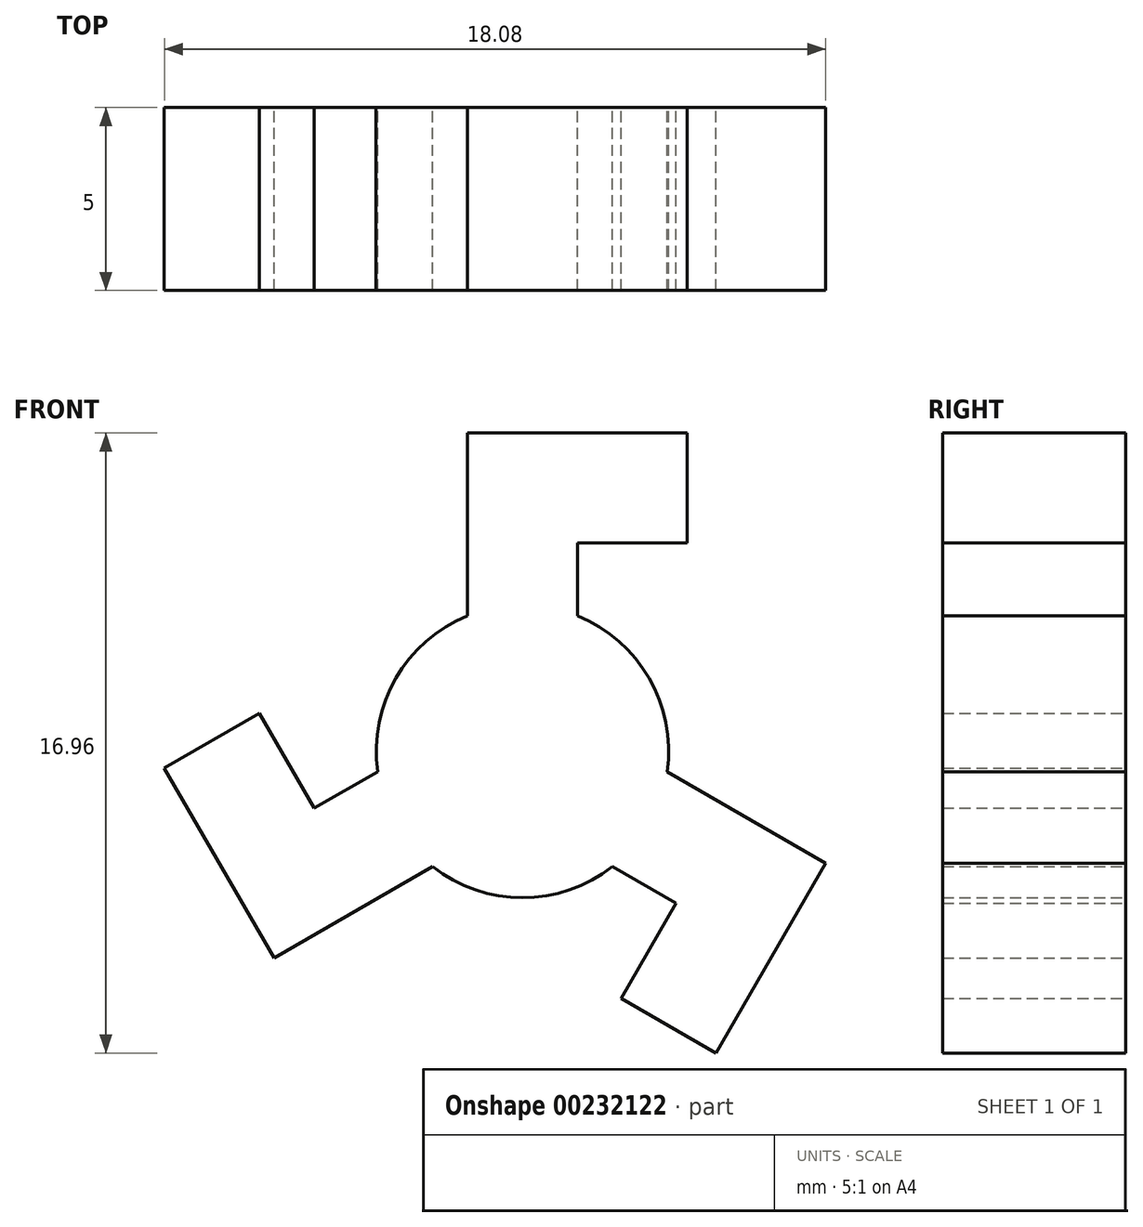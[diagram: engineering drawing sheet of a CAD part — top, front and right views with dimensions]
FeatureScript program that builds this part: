
annotation { "Feature Type Name" : "Feature", "Feature Type Description" : "" }
export const myFeature = defineFeature(function(context is Context, id is Id, definition is map)
    precondition{}
    {
        {
            var Q0;
            Q0=qCreatedBy(makeId("Front.planeOp"),FACE);
            var sketch = newSketch(context, id + "F0", { "sketchPlane" : qUnion([Q0])});
            skArc(sketch, "E0", {"start": v(-1.5, 3.7) * mm, "mid": v(-3.46, 2) * mm, "end": v(-3.96, -0.56) * mm});
            skLineSegment(sketch, "E1.left", {"start": v(-1.5, 8.4) * mm, "end": v(-1.5, 3.7) * mm});
            skLineSegment(sketch, "E1.right", {"start": v(1.5, 5.7) * mm, "end": v(1.5, 3.7) * mm});
            skPoint(sketch, "E1.middle", {"position": v(0, 4) * mm});
            skLineSegment(sketch, "E2.bottom", {"start": v(1.5, 5.7) * mm, "end": v(4.5, 5.7) * mm});
            skLineSegment(sketch, "E2.top", {"start": v(-1.5, 8.7) * mm, "end": v(4.5, 8.7) * mm});
            skLineSegment(sketch, "E2.left", {"start": v(-1.5, 8.4) * mm, "end": v(-1.5, 8.7) * mm});
            skLineSegment(sketch, "E2.right", {"start": v(4.5, 5.7) * mm, "end": v(4.5, 8.7) * mm});
            skPoint(sketch, "E2.middle", {"position": v(1.5, 7.2) * mm});
            skPoint(sketch, "E1.top.start.orphan", {"position": v(-1.5, 0.8) * mm});
            skPoint(sketch, "E3.orphan", {"position": v(1.5, -0.4) * mm});
            skPoint(sketch, "E4.orphan", {"position": v(-1.5, 5.7) * mm});
            skLineSegment(sketch, "E5.1.0", {"start": v(-6.8, -5.65) * mm, "end": v(-9.8, -0.46) * mm});
            skLineSegment(sketch, "E5.1.1", {"start": v(-7.2, 1.04) * mm, "end": v(-9.8, -0.46) * mm});
            skPoint(sketch, "E5.1.2", {"position": v(-7, -2.3) * mm});
            skLineSegment(sketch, "E5.1.3", {"start": v(-5.7, -1.56) * mm, "end": v(-7.2, 1.04) * mm});
            skPoint(sketch, "E5.1.4", {"position": v(-4.2, -4.15) * mm});
            skPoint(sketch, "E5.1.5", {"position": v(-3.46, -2) * mm});
            skLineSegment(sketch, "E5.1.6", {"start": v(-5.7, -1.56) * mm, "end": v(-3.96, -0.56) * mm});
            skLineSegment(sketch, "E5.1.7", {"start": v(-6.52, -5.5) * mm, "end": v(-2.46, -3.15) * mm});
            skLineSegment(sketch, "E5.1.8", {"start": v(-6.52, -5.5) * mm, "end": v(-6.8, -5.65) * mm});
            skLineSegment(sketch, "E5.2.0", {"start": v(8.3, -3.06) * mm, "end": v(5.3, -8.25) * mm});
            skLineSegment(sketch, "E5.2.1", {"start": v(2.7, -6.75) * mm, "end": v(5.3, -8.25) * mm});
            skPoint(sketch, "E5.2.2", {"position": v(5.5, -4.9) * mm});
            skLineSegment(sketch, "E5.2.3", {"start": v(4.2, -4.15) * mm, "end": v(2.7, -6.75) * mm});
            skPoint(sketch, "E5.2.4", {"position": v(5.7, -1.56) * mm});
            skPoint(sketch, "E5.2.5", {"position": v(3.46, -2) * mm});
            skLineSegment(sketch, "E5.2.6", {"start": v(4.2, -4.15) * mm, "end": v(2.46, -3.15) * mm});
            skLineSegment(sketch, "E5.2.7", {"start": v(8.02, -2.9) * mm, "end": v(3.96, -0.56) * mm});
            skLineSegment(sketch, "E5.2.8", {"start": v(8.02, -2.9) * mm, "end": v(8.3, -3.06) * mm});
            skArc(sketch, "E6.trimOffspring", {"start": v(-2.46, -3.15) * mm, "mid": v(0, -4) * mm, "end": v(2.46, -3.15) * mm});
            skArc(sketch, "E7.trimOffspring", {"start": v(3.96, -0.56) * mm, "mid": v(3.46, 2) * mm, "end": v(1.5, 3.7) * mm});
            skSolve(sketch);
        }
        {
            var Q0;
            Q0 = qSketchRegion(id + "F0", true);
            extrude(context, id + "F1", {"entities" : qUnion([Q0]), "depth" : 5 * mm});
        }
    });
